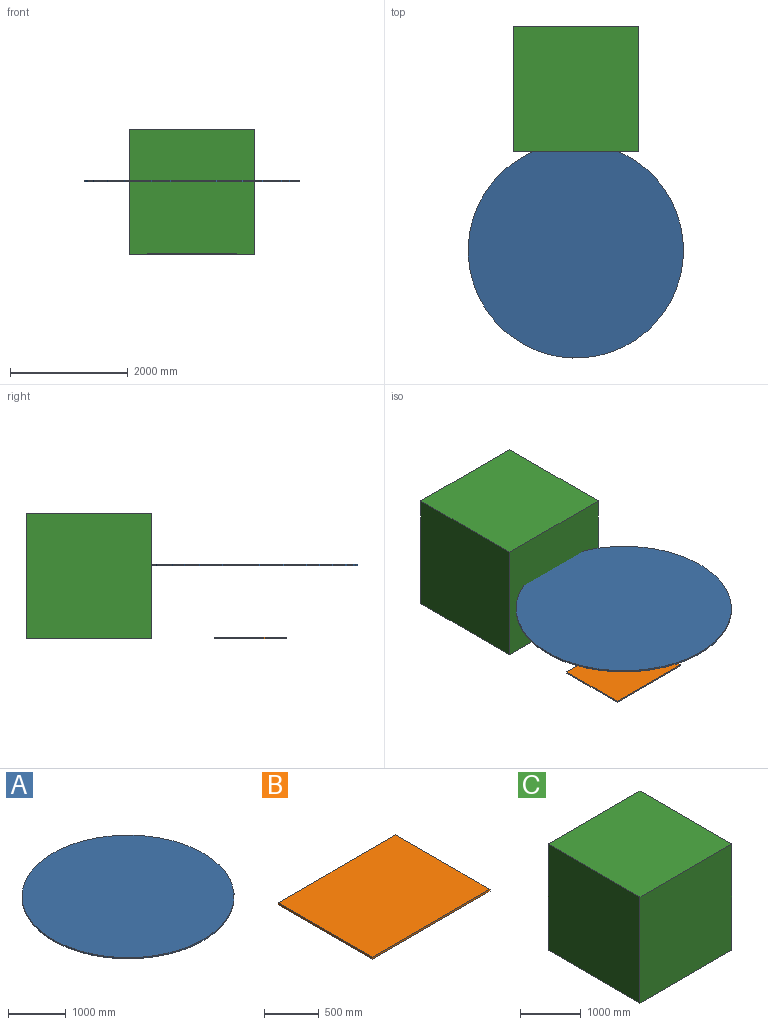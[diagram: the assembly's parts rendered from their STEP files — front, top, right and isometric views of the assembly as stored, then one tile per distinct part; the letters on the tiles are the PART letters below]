
ASSEMBLY  parts=3 mates=1
PART A: 3 faces, bbox 3657.6x3657.6x25.4 mm
  f0: cylinder r=1828.8mm len=3657.6mm, axis (0,0,-1), area 291863.5mm2, adj f1,f2
  f1: plane 3657.6x3657.6mm, normal (0,0,1), area 10507086.3mm2, adj f0
  f2: plane 3657.6x3657.6mm, normal (0,0,-1), area 10507086.3mm2, adj f0
PART B: 6 faces, bbox 1524x1219.2x22.2 mm
  f0: plane 1524x22.23mm, normal (0,-1,0), area 33870.9mm2, adj f1,f3,f4,f5
  f1: plane 1219.2x22.23mm, normal (1,0,0), area 27096.7mm2, adj f0,f2,f4,f5
  f2: plane 1524x22.23mm, normal (0,1,0), area 33870.9mm2, adj f1,f3,f4,f5
  f3: plane 1219.2x22.23mm, normal (-1,0,0), area 27096.7mm2, adj f0,f2,f4,f5
  f4: plane 1524x1219.2mm, normal (0,0,1), area 1858060.8mm2, adj f0,f1,f2,f3
  f5: plane 1524x1219.2mm, normal (0,0,-1), area 1858060.8mm2, adj f0,f1,f2,f3
PART C: 6 faces, bbox 2133.6x2133.6x2133.6 mm
  f0: plane 2133.6x2133.6mm, normal (1,0,0), area 4552249mm2, adj f1,f3,f4,f5
  f1: plane 2133.6x2133.6mm, normal (0,1,0), area 4552249mm2, adj f0,f2,f4,f5
  f2: plane 2133.6x2133.6mm, normal (-1,0,0), area 4552249mm2, adj f1,f3,f4,f5
  f3: plane 2133.6x2133.6mm, normal (0,-1,0), area 4552249mm2, adj f0,f2,f4,f5
  f4: plane 2133.6x2133.6mm, normal (0,0,1), area 4552249mm2, adj f0,f1,f2,f3
  f5: plane 2133.6x2133.6mm, normal (0,0,-1), area 4552249mm2, adj f0,f1,f2,f3
PLACE A t=(0,-2743.2,1241.42)mm
PLACE B t=(0,-2743.2,0)mm
PLACE C at identity
MATE fastened B.f4 <-> A.f0  axis (0,0,1) through (0,-2743.2,22.22)mm
